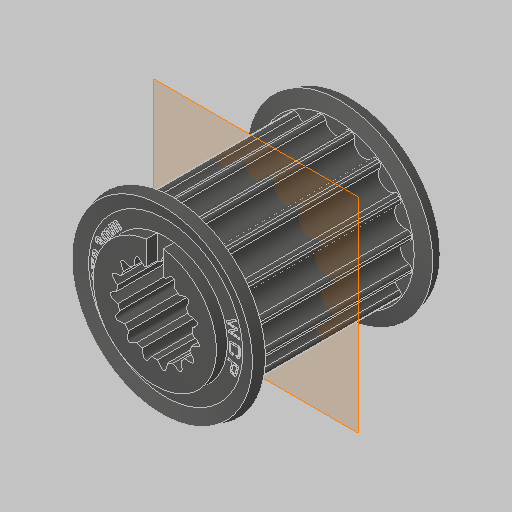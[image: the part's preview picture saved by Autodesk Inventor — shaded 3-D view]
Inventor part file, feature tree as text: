
AUTODESK INVENTOR PART (.ipt)
format: ipt  version: 2023.5 (Build 275446000, 446)  size: 683,008 bytes
history: native  units: in
note: dims shown in document units (in); Inventor stores cm internally (conversion verified against a paired STEP export)
features: other x2, mirror x1
ambient origin geometry x8: Origin, YZ Plane, XZ Plane, XY Plane, X Axis, Y Axis, Z Axis, Center Point
bodies: Solid1 (feature_tree), Solid2 (feature_tree), Solid3 (feature_tree)
feature tree (3):
  mirror  "Mirror3"
  other  "Cut-Extrude1"
  other  "Cut-Extrude2"
